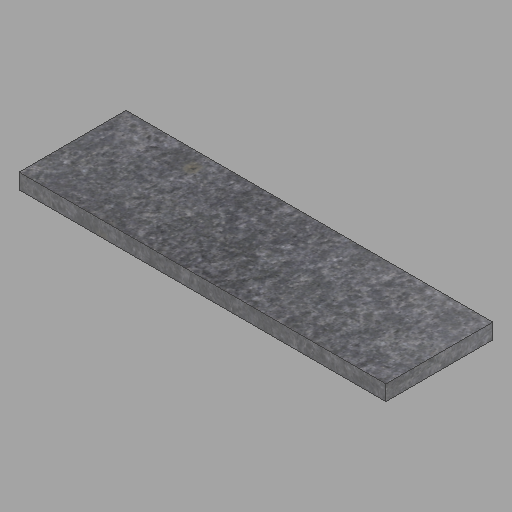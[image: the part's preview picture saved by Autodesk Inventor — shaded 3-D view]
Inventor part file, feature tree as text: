
AUTODESK INVENTOR PART (.ipt)
format: ipt  version: 2023 (Build 270158000, 158)  size: 203,264 bytes
history: native  units: in
note: dims shown in document units (in); Inventor stores cm internally (conversion verified against a paired STEP export)
features: other x1, extrude x1, sketch x1
ambient origin geometry x8: Origin, YZ Plane, XZ Plane, XY Plane, X Axis, Y Axis, Z Axis, Center Point
bodies: Solid1 (feature_tree)
feature tree (3):
  other  "2x14x48-2"
  extrude  "Extrusion1"  Depth=14.0in
  sketch  "Sketch1"  dims[d0=2.0in d1=14.0in d2=48.0in d3=0.0in]
